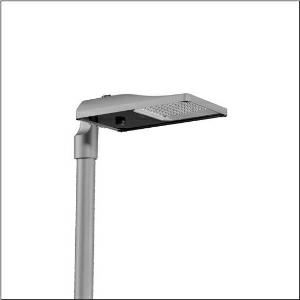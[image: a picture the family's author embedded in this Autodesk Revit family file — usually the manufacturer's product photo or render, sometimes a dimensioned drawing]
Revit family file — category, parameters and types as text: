
# Revit family: streetlight_sl_31_midi___st0_5a_5xh7b31t08la_752d
name_source: partatom
category: Lighting Fixtures
units: mm (PartAtom-declared; Revit-internal decimal feet)

## family parameters
Cut with Voids When Loaded = No
Host = Face
Light Source = No
Part Type = Normal
Room Calculation Point = No
Round Connector Dimension = Use Diameter
Shared = No

## types (1)
- --- (1 x LED, 13170 lm, 86.5 W, 3000K)
    Apparent Load = 87 VA
    CIE Flux Codes = 41 75 97 100 100
    Color Rendering = 70
    Color Temperature = 3000K
    Default Elevation = 1800 mm
    Description = Streetlight SL 31 midi D4i, Desk-Remote mast luminaire for post-top, side-entry; light control with lens of PMMA; light distribution: ST0.5a, direct asymmetric distribution, for standard-compliant lighting for roads and squares; LED: luminous flux: 13.170lm, light colour: 730, colour temperature: 3000K; luminous efficacy: 152,3lm/W; control: pre-setting: logarithmic dimming characteristic, flexible luminous flux parameterisation, time-dependent luminous flux control, constant luminous flux control, power reduction, intelligent temperature release in ECG and LED module, overheat protection; luminaire housing, of diecast aluminium, SITECO metallic grey (DB 702S), corrosivity category C5 high according to DIN EN ISO 12944; cover of toughened safety glass, transparent, opened without tools; mast flange of diecast aluminium, SITECO metallic grey (DB 702S), spigot size: 76/60mm, mast flange included unmounted; cable length: 10,5m, connection cable pre-assembled; mains connection: 220..240V, AC, 50/60Hz; power consumption (at start of service life): 86,5W / (at end of service life): 90W / (with reduced operation 50%): 39,6W; protection rating (complete): IP66; insulation class (complete): insulation class II (safety insulation); impact resistance: IK09; certification: CE, ENEC, ENEC+, VDE, UKCA, ZD4i; permissible operating ambient temperature for outdoor applications: -40..+50°C; packaging unit: 1 piece

Light Distribution: ST0.5a
    Height = 79 mm
    Lamp = 1 x LED
    Lamp Light Flux = 13170 lm
    Lamp Power = 86.5 W
    Lamp count = 1
    Length = 577 mm
    Luminous efficacy = 152 lm/W
    Manufacturer = Siteco
    ModVariant = No
    Model = 5XH7B31T08LA
    Number of Poles = 1
    OnlyDefault = Yes
    Power Factor = 1
    Product Name = Streetlight SL 31 midi | ST0.5a
    Product group = mast luminaire | pylon top
    ProductGroupID = 6100
    Protection Class = Protection class II
    Protection Degree = IP 66
    RLX_Detail_Level = 1
    RLX_Emergency_Light_Flux = 0 lm
    RLX_Emergency_Type = 0
    RLX_Emergency_Type_DB = No
    RlxData = <blob elided: 53597 chars, md5=9672144e>
    Socket = socket
    Standby Power = 0 W
    System Light Flux = 13170 lm
    System Power = 87 W
    Type Comments = factory setting: luminous flux: 100 % | dim-lin: 254 | 456 mA
    Type Image = l_1300321.jpg
    URL = http://relux.com
    VarID = @adj_064463
    Voltage = 0 V
    Weight = 0.00 kg
    Width = 362 mm

## geometry (parser evidence)
native form markers: Blend x4, Sweep x10
no freeform markers — native parametric forms only
